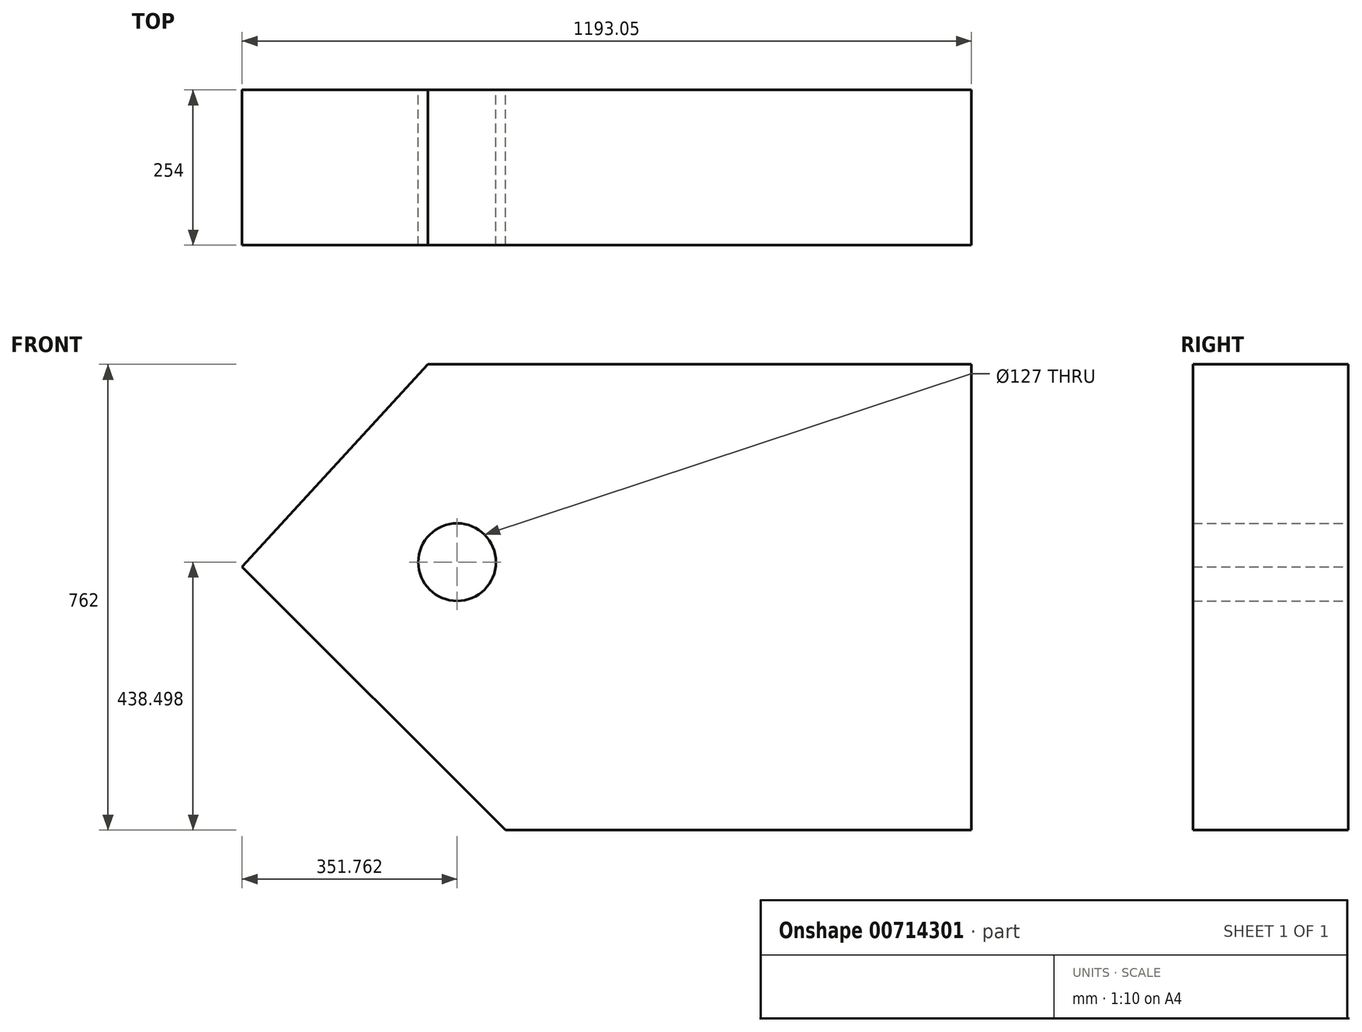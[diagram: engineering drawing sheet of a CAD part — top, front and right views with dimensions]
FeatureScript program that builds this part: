
annotation { "Feature Type Name" : "Feature", "Feature Type Description" : "" }
export const myFeature = defineFeature(function(context is Context, id is Id, definition is map)
    precondition{}
    {
        {
            var Q0;
            Q0=qCreatedBy(makeId("Front.planeOp"),FACE);
            var sketch = newSketch(context, id + "F0", { "sketchPlane" : qUnion([Q0])});
            skLineSegment(sketch, "E0", {"start": v(0, 0) * mm, "end": v(762, 0) * mm});
            skLineSegment(sketch, "E1", {"start": v(762, 0) * mm, "end": v(762, 762) * mm});
            skLineSegment(sketch, "E2", {"start": v(762, 762) * mm, "end": v(-127, 762) * mm});
            skLineSegment(sketch, "E3", {"start": v(0, 0) * mm, "end": v(-431.05, 431.05) * mm});
            skLineSegment(sketch, "E4", {"start": v(-431.05, 431.05) * mm, "end": v(-127, 762) * mm});
            skCircle(sketch, "E5", {"center": v(-79.29, 438.5) * mm, "radius": 63.5 * mm});
            skSolve(sketch);
        }
        {
            var Q0;
            Q0=makeQuery(id+"F0.imprint","IMPRINT",FACE,{"disambiguationData":[TD([[makeQuery(id+"F0.imprint","IMPRINT",EDGE,{"derivedFrom":sQuery(id+"F0.wireOp",EDGE,"E0")}),1.0]])]});
            extrude(context, id + "F1", {"entities" : qUnion([Q0]), "depth" : 254 * mm, "offsetDistance" : 25.4 * mm});
        }
    });
